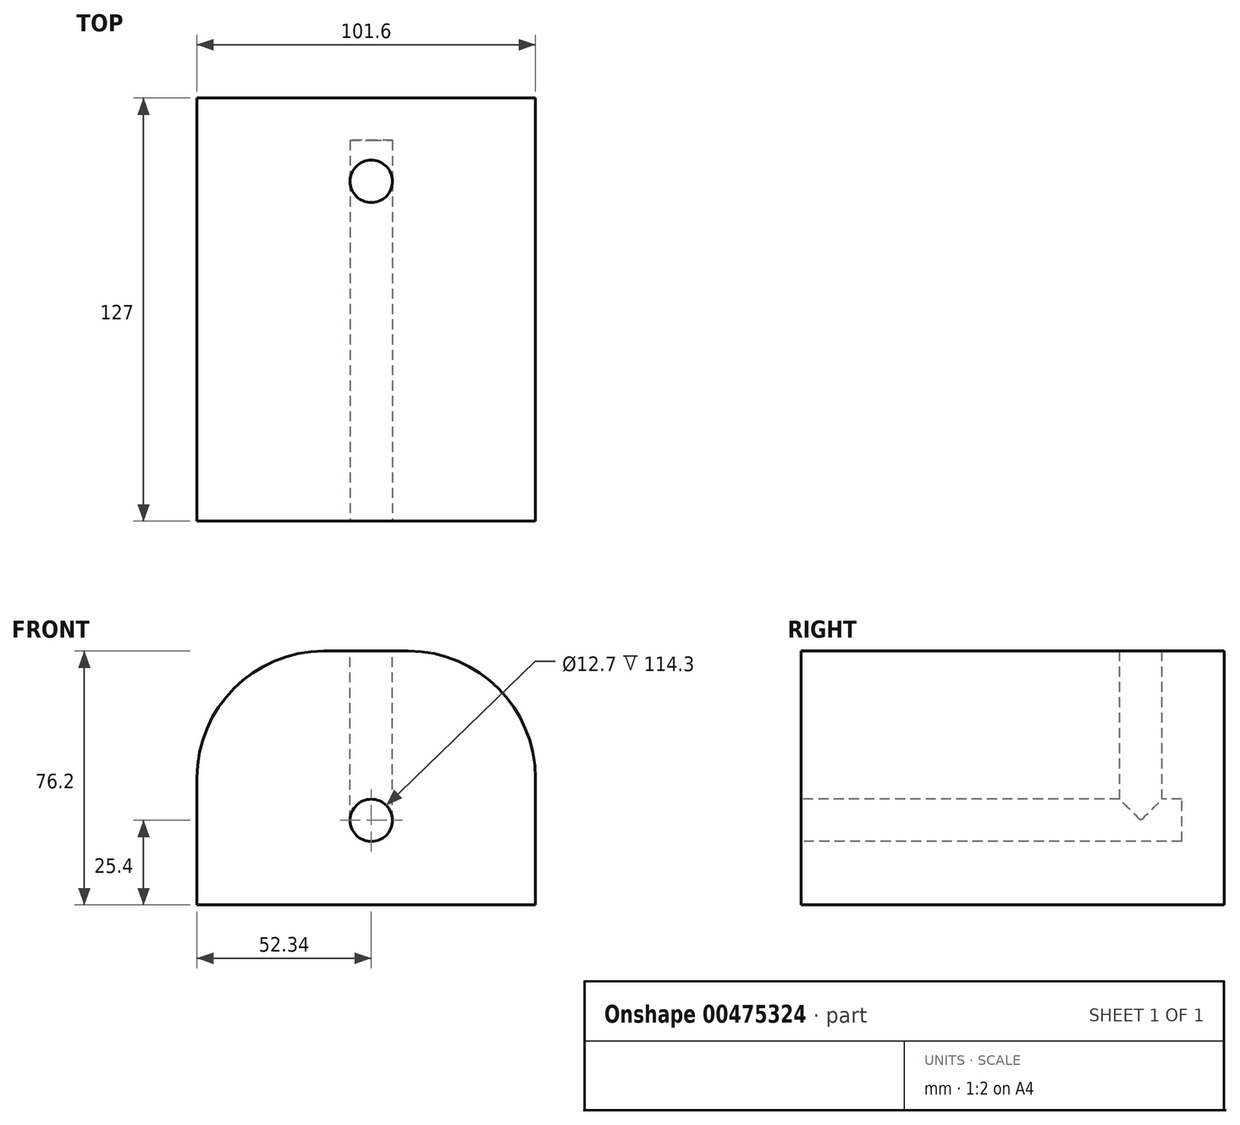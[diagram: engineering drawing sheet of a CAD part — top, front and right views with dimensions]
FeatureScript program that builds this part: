
annotation { "Feature Type Name" : "Feature", "Feature Type Description" : "" }
export const myFeature = defineFeature(function(context is Context, id is Id, definition is map)
    precondition{}
    {
        {
            var Q0;
            Q0=qCreatedBy(makeId("Top.planeOp"),FACE);
            var sketch = newSketch(context, id + "F0", { "sketchPlane" : qUnion([Q0])});
            skLineSegment(sketch, "E0.bottom", {"start": v(-52.34, 66.75) * mm, "end": v(49.26, 66.75) * mm});
            skLineSegment(sketch, "E0.top", {"start": v(-52.34, -60.25) * mm, "end": v(49.26, -60.25) * mm});
            skLineSegment(sketch, "E0.left", {"start": v(-52.34, 66.75) * mm, "end": v(-52.34, -60.25) * mm});
            skLineSegment(sketch, "E0.right", {"start": v(49.26, 66.75) * mm, "end": v(49.26, -60.25) * mm});
            skSolve(sketch);
        }
        {
            var Q0;
            Q0=makeQuery(id+"F0.imprint","IMPRINT",FACE,{"disambiguationData":[TD([[makeQuery(id+"F0.imprint","IMPRINT",EDGE,{"derivedFrom":sQuery(id+"F0.wireOp",EDGE,"E0.bottom")}),-1.0]])]});
            extrude(context, id + "F1", {"entities" : qUnion([Q0]), "depth" : 76.2 * mm});
        }
        {
            var Q0;
            Q0=makeQuery(id+"F1.opExtrude","CAP_EDGE",EDGE,{"disambiguationData":[OSD([sQuery(id+"F0.wireOp",EDGE,"E0.left")])],"isStart":false});
            var Q1;
            Q1=makeQuery(id+"F1.opExtrude","CAP_EDGE",EDGE,{"disambiguationData":[OSD([sQuery(id+"F0.wireOp",EDGE,"E0.right")])],"isStart":false});
            fillet(context, id + "F2", {"entities" : qUnion([Q0, Q1]), "radius" : 38.1 * mm, "tangentPropagation" : true, "allowEdgeOverflow" : false});
        }
        {
            var Q0;
            Q0=makeQuery(id+"F1.opExtrude","SWEPT_FACE",FACE,{"disambiguationData":[OSD([sQuery(id+"F0.wireOp",EDGE,"E0.top")])]});
            var sketch = newSketch(context, id + "F3", { "sketchPlane" : qUnion([Q0])});
            skCircle(sketch, "E1", {"center": v(0, 25.4) * mm, "radius": 6.35 * mm});
            skSolve(sketch);
        }
        {
            var Q0;
            Q0=makeQuery(id+"F3.imprint","IMPRINT",FACE,{"disambiguationData":[TD([[makeQuery(id+"F3.imprint","IMPRINT",EDGE,{"derivedFrom":sQuery(id+"F3.wireOp",EDGE,"E1")}),1.0]])]});
            extrude(context, id + "F4", {"entities" : qUnion([Q0]), "operationType" : NewBodyOperationType.REMOVE, "oppositeDirection" : true, "depth" : 114.3 * mm});
        }
        {
            var Q0;
            Q0=makeQuery(id+"F1.opExtrude","CAP_FACE",FACE,{"disambiguationData":[OSD([sQuery(id+"F0.wireOp",EDGE,"E0.bottom"),sQuery(id+"F0.wireOp",EDGE,"E0.top"),sQuery(id+"F0.wireOp",EDGE,"E0.left"),sQuery(id+"F0.wireOp",EDGE,"E0.right")])],"isStart":false});
            var sketch = newSketch(context, id + "F5", { "sketchPlane" : qUnion([Q0])});
            skCircle(sketch, "E2", {"center": v(0, 41.73) * mm, "radius": 6.35 * mm});
            skSolve(sketch);
        }
        {
            var Q0;
            Q0=makeQuery(id+"F5.imprint","IMPRINT",FACE,{"disambiguationData":[TD([[makeQuery(id+"F5.imprint","IMPRINT",EDGE,{"derivedFrom":sQuery(id+"F5.wireOp",EDGE,"E2")}),1.0]])]});
            extrude(context, id + "F6", {"entities" : qUnion([Q0]), "operationType" : NewBodyOperationType.REMOVE, "oppositeDirection" : true, "depth" : 50.8 * mm});
        }
    });
